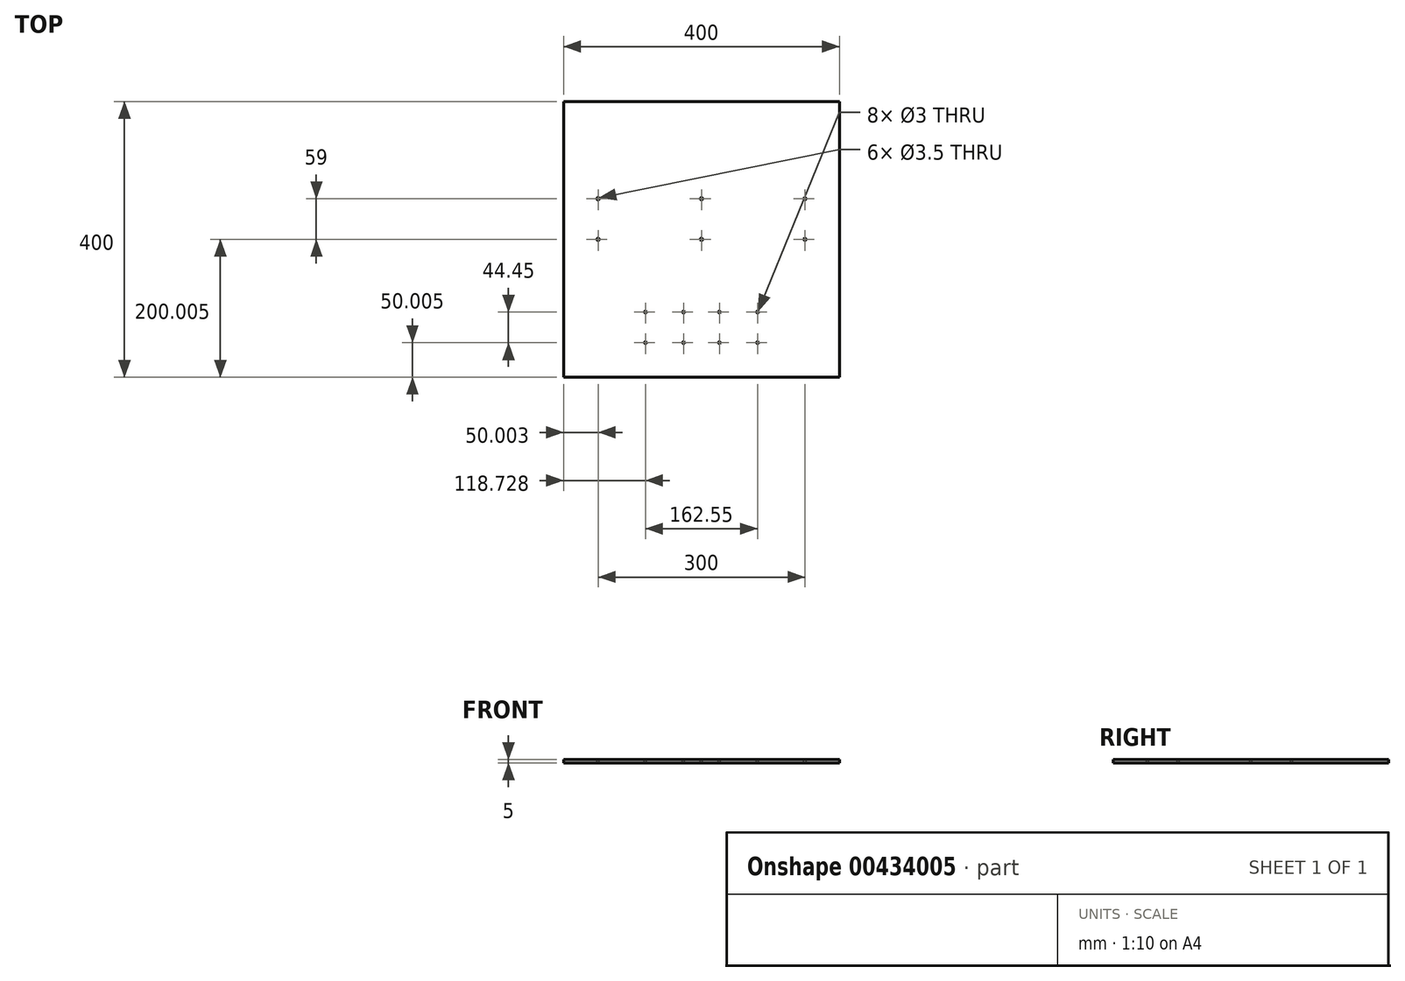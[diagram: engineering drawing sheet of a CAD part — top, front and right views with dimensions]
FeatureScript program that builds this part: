
annotation { "Feature Type Name" : "Feature", "Feature Type Description" : "" }
export const myFeature = defineFeature(function(context is Context, id is Id, definition is map)
    precondition{}
    {
        {
            var Q0;
            Q0=qCreatedBy(makeId("Top.planeOp"),FACE);
            var sketch = newSketch(context, id + "F0", { "sketchPlane" : qUnion([Q0])});
            skLineSegment(sketch, "E0.bottom", {"start": v(-197.38, 325.18) * mm, "end": v(202.62, 325.18) * mm});
            skLineSegment(sketch, "E0.top", {"start": v(-197.38, -74.82) * mm, "end": v(202.62, -74.82) * mm});
            skLineSegment(sketch, "E0.left", {"start": v(-197.38, 325.18) * mm, "end": v(-197.38, -74.82) * mm});
            skLineSegment(sketch, "E0.right", {"start": v(202.62, 325.18) * mm, "end": v(202.62, -74.82) * mm});
            skSolve(sketch);
        }
        {
            var Q0;
            Q0 = qSketchRegion(id + "F0", true);
            extrude(context, id + "F1", {"entities" : qUnion([Q0]), "depth" : 5 * mm});
        }
        {
            var Q0;
            Q0=makeQuery(id+"F1.opExtrude","CAP_FACE",FACE,{"disambiguationData":[OSD([sQuery(id+"F0.wireOp",EDGE,"E0.bottom"),sQuery(id+"F0.wireOp",EDGE,"E0.top"),sQuery(id+"F0.wireOp",EDGE,"E0.left"),sQuery(id+"F0.wireOp",EDGE,"E0.right")])],"isStart":false});
            var sketch = newSketch(context, id + "F2", { "sketchPlane" : qUnion([Q0])});
            skCircle(sketch, "E1", {"center": v(-147.38, 125.18) * mm, "radius": 1.75 * mm});
            skCircle(sketch, "E2.0.1.0", {"center": v(-147.38, 184.18) * mm, "radius": 1.75 * mm});
            skCircle(sketch, "E2.1.0.0", {"center": v(2.62, 125.18) * mm, "radius": 1.75 * mm});
            skCircle(sketch, "E2.1.1.0", {"center": v(2.62, 184.18) * mm, "radius": 1.75 * mm});
            skCircle(sketch, "E2.2.0.0", {"center": v(152.62, 125.18) * mm, "radius": 1.75 * mm});
            skCircle(sketch, "E2.2.1.0", {"center": v(152.62, 184.18) * mm, "radius": 1.75 * mm});
            skLineSegment(sketch, "E2.direction1", {"start": v(-147.38, 125.18) * mm, "end": v(2.62, 125.18) * mm, "construction": true});
            skLineSegment(sketch, "E2.direction2", {"start": v(-147.38, 125.18) * mm, "end": v(-147.38, 184.18) * mm, "construction": true});
            skSolve(sketch);
        }
        {
            var Q0;
            Q0 = qSketchRegion(id + "F2", true);
            extrude(context, id + "F3", {"entities" : qUnion([Q0]), "operationType" : NewBodyOperationType.REMOVE, "endBound" : BoundingType.THROUGH_ALL, "oppositeDirection" : true, "depth" : 25 * mm});
        }
        {
            var Q0;
            Q0=makeQuery(id+"F1.opExtrude","CAP_FACE",FACE,{"disambiguationData":[OSD([sQuery(id+"F0.wireOp",EDGE,"E0.bottom"),sQuery(id+"F0.wireOp",EDGE,"E0.top"),sQuery(id+"F0.wireOp",EDGE,"E0.left"),sQuery(id+"F0.wireOp",EDGE,"E0.right")])],"isStart":false});
            var sketch = newSketch(context, id + "F4", { "sketchPlane" : qUnion([Q0])});
            skCircle(sketch, "E3", {"center": v(-23.38, -24.82) * mm, "radius": 1.5 * mm});
            skCircle(sketch, "E4.0.1.0", {"center": v(-23.38, 19.63) * mm, "radius": 1.5 * mm});
            skCircle(sketch, "E4.1.0.0", {"center": v(28.62, -24.82) * mm, "radius": 1.5 * mm});
            skCircle(sketch, "E4.1.1.0", {"center": v(28.62, 19.63) * mm, "radius": 1.5 * mm});
            skLineSegment(sketch, "E4.direction1", {"start": v(-23.38, -24.82) * mm, "end": v(28.62, -24.82) * mm, "construction": true});
            skLineSegment(sketch, "E4.direction2", {"start": v(-23.38, -24.82) * mm, "end": v(-23.38, 19.63) * mm, "construction": true});
            skSolve(sketch);
        }
        {
            var Q0;
            Q0 = qSketchRegion(id + "F4", true);
            extrude(context, id + "F5", {"entities" : qUnion([Q0]), "operationType" : NewBodyOperationType.REMOVE, "endBound" : BoundingType.THROUGH_ALL, "oppositeDirection" : true, "depth" : 25 * mm});
        }
        {
            var Q0;
            Q0=makeQuery(id+"F1.opExtrude","CAP_FACE",FACE,{"disambiguationData":[OSD([sQuery(id+"F0.wireOp",EDGE,"E0.bottom"),sQuery(id+"F0.wireOp",EDGE,"E0.top"),sQuery(id+"F0.wireOp",EDGE,"E0.left"),sQuery(id+"F0.wireOp",EDGE,"E0.right")])],"isStart":false});
            var sketch = newSketch(context, id + "F6", { "sketchPlane" : qUnion([Q0])});
            skCircle(sketch, "E5", {"center": v(-78.65, -24.82) * mm, "radius": 1.5 * mm});
            skCircle(sketch, "E6.0.1.0", {"center": v(-78.65, 19.63) * mm, "radius": 1.5 * mm});
            skCircle(sketch, "E6.1.0.0", {"center": v(83.9, -24.82) * mm, "radius": 1.5 * mm});
            skCircle(sketch, "E6.1.1.0", {"center": v(83.9, 19.63) * mm, "radius": 1.5 * mm});
            skLineSegment(sketch, "E6.direction1", {"start": v(-78.65, -24.82) * mm, "end": v(83.9, -24.82) * mm, "construction": true});
            skLineSegment(sketch, "E6.direction2", {"start": v(-78.65, -24.82) * mm, "end": v(-78.65, 19.63) * mm, "construction": true});
            skSolve(sketch);
        }
        {
            var Q0;
            Q0 = qSketchRegion(id + "F6", true);
            extrude(context, id + "F7", {"entities" : qUnion([Q0]), "operationType" : NewBodyOperationType.REMOVE, "endBound" : BoundingType.THROUGH_ALL, "oppositeDirection" : true, "depth" : 25 * mm});
        }
    });
